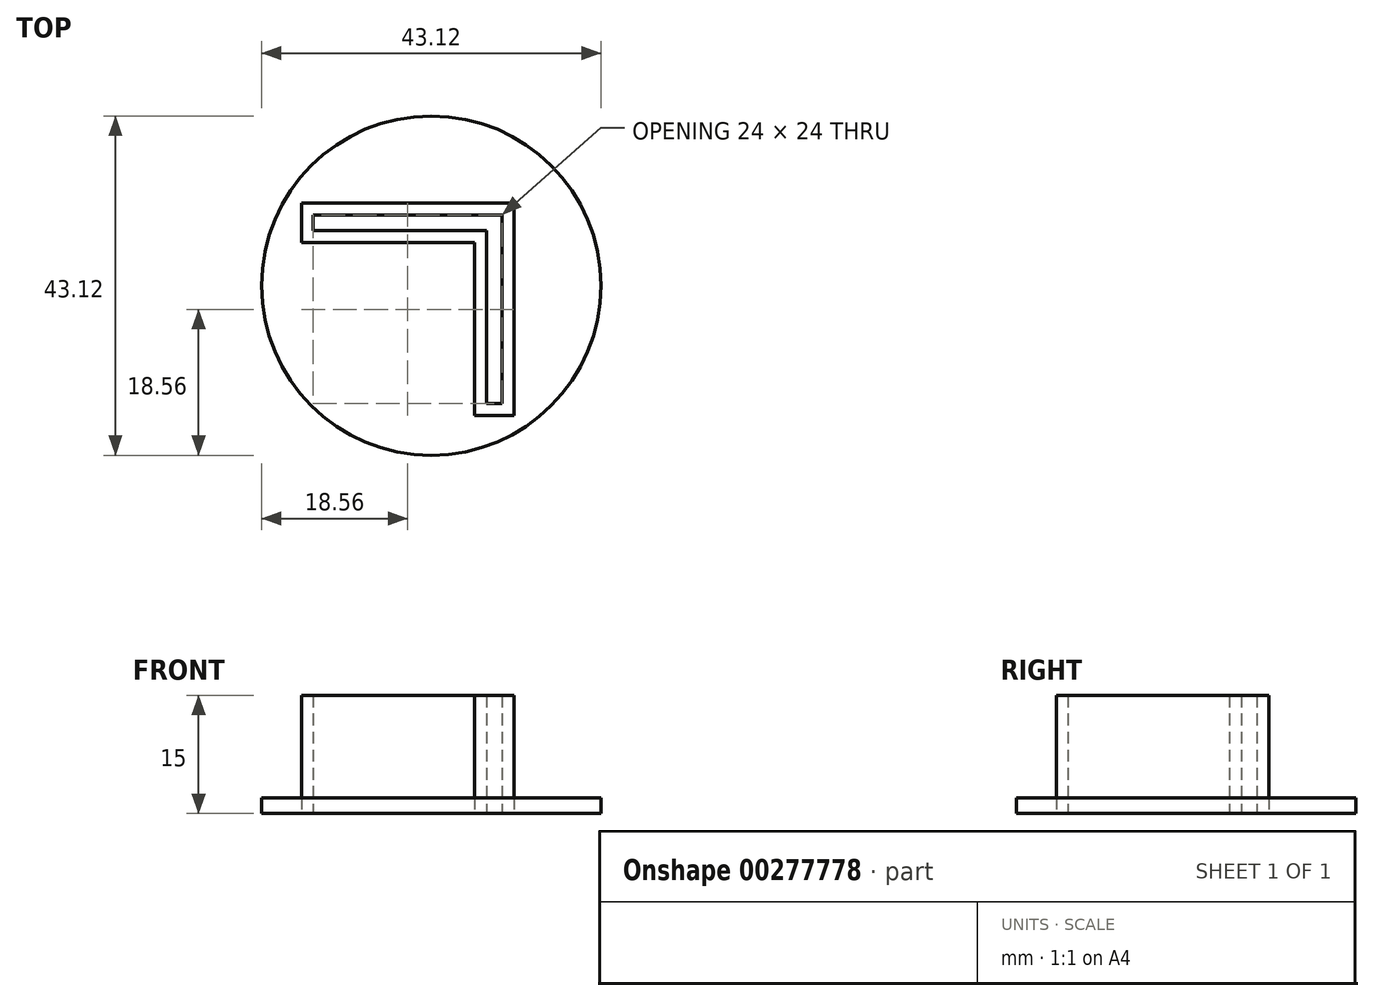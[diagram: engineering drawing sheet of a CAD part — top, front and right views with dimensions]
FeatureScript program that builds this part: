
annotation { "Feature Type Name" : "Feature", "Feature Type Description" : "" }
export const myFeature = defineFeature(function(context is Context, id is Id, definition is map)
    precondition{}
    {
        {
            var Q0;
            Q0=qCreatedBy(makeId("Top.planeOp"),FACE);
            var sketch = newSketch(context, id + "F0", { "sketchPlane" : qUnion([Q0])});
            skLineSegment(sketch, "E0.bottom", {"start": v(-12, 12) * mm, "end": v(12, 12) * mm});
            skLineSegment(sketch, "E0.top", {"start": v(10, -12) * mm, "end": v(12, -12) * mm});
            skLineSegment(sketch, "E0.left", {"start": v(-12, 12) * mm, "end": v(-12, 10) * mm});
            skLineSegment(sketch, "E0.right", {"start": v(12, 12) * mm, "end": v(12, -12) * mm});
            skPoint(sketch, "E0.middle", {"position": v(0, 0) * mm});
            skLineSegment(sketch, "E1.bottom", {"start": v(-10, 10) * mm, "end": v(10, 10) * mm});
            skLineSegment(sketch, "E1.right", {"start": v(10, 10) * mm, "end": v(10, -10) * mm});
            skLineSegment(sketch, "E2", {"start": v(-10, 10) * mm, "end": v(-12, 10) * mm});
            skLineSegment(sketch, "E3", {"start": v(10, -10) * mm, "end": v(10, -12) * mm});
            skPoint(sketch, "E1.left.end.orphan", {"position": v(-10, -10) * mm});
            skPoint(sketch, "E4.orphan", {"position": v(-12, -12) * mm});
            skLineSegment(sketch, "E5.bottom", {"start": v(13.5, 13.5) * mm, "end": v(-13.5, 13.5) * mm});
            skLineSegment(sketch, "E5.top", {"start": v(13.5, -13.5) * mm, "end": v(8.5, -13.5) * mm});
            skLineSegment(sketch, "E5.left", {"start": v(13.5, 13.5) * mm, "end": v(13.5, -13.5) * mm});
            skLineSegment(sketch, "E5.right", {"start": v(-13.5, 13.5) * mm, "end": v(-13.5, 8.5) * mm});
            skLineSegment(sketch, "E6.bottom", {"start": v(8.5, 8.5) * mm, "end": v(-8.5, 8.5) * mm});
            skLineSegment(sketch, "E6.left", {"start": v(8.5, 8.5) * mm, "end": v(8.5, -8.5) * mm});
            skLineSegment(sketch, "E7", {"start": v(-8.5, 8.5) * mm, "end": v(-13.5, 8.5) * mm});
            skLineSegment(sketch, "E8", {"start": v(8.5, -8.5) * mm, "end": v(8.5, -13.5) * mm});
            skPoint(sketch, "E6.top.end.orphan", {"position": v(-8.5, -8.5) * mm});
            skPoint(sketch, "E9.orphan", {"position": v(-13.5, -13.5) * mm});
            skPoint(sketch, "E10", {"position": v(6, 6) * mm});
            skPoint(sketch, "E11", {"position": v(3, 3) * mm});
            skCircle(sketch, "E12", {"center": v(3, 3) * mm, "radius": 19.56 * mm, "construction": true});
            skLineSegment(sketch, "E13.trimOffspring", {"start": v(8.5, 8.5) * mm, "end": v(10, 10) * mm, "construction": true});
            skCircle(sketch, "E14", {"center": v(3, 3) * mm, "radius": 21.56 * mm});
            skSolve(sketch);
        }
        {
            var Q0;
            Q0 = qSketchRegion(id + "F0", true);
            var Q1;
            Q1=makeQuery(id+"F0.imprint","IMPRINT",FACE,{"disambiguationData":[TD([[makeQuery(id+"F0.imprint","IMPRINT",EDGE,{"derivedFrom":sQuery(id+"F0.wireOp",EDGE,"E0.bottom")}),-1.0]])]});
            var Q2;
            Q2=makeQuery(id+"F0.imprint","IMPRINT",FACE,{"disambiguationData":[TD([[makeQuery(id+"F0.imprint","IMPRINT",EDGE,{"derivedFrom":sQuery(id+"F0.wireOp",EDGE,"E0.bottom")}),1.0]])]});
            extrude(context, id + "F1", {"entities" : qUnion([Q0, Q1, Q2]), "depth" : 2 * mm});
        }
        {
            var Q0;
            Q0=makeQuery(id+"F0.imprint","IMPRINT",FACE,{"disambiguationData":[TD([[makeQuery(id+"F0.imprint","IMPRINT",EDGE,{"derivedFrom":sQuery(id+"F0.wireOp",EDGE,"E0.bottom")}),1.0]])]});
            extrude(context, id + "F2", {"entities" : qUnion([Q0]), "depth" : 15 * mm});
        }
    });
